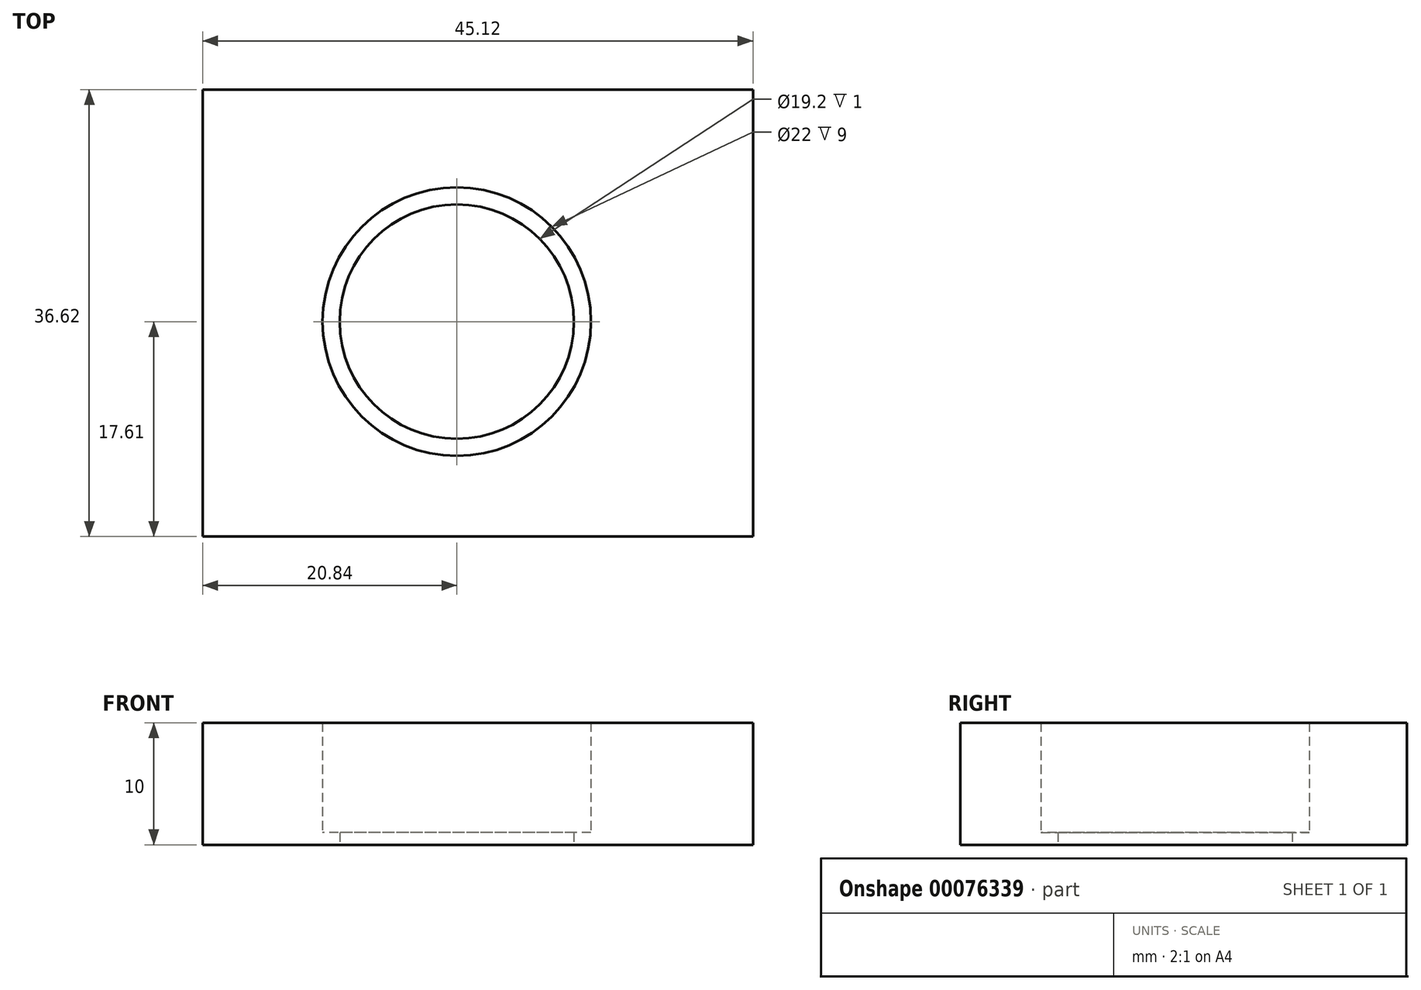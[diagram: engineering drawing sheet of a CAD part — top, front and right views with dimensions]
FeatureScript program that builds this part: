
annotation { "Feature Type Name" : "Feature", "Feature Type Description" : "" }
export const myFeature = defineFeature(function(context is Context, id is Id, definition is map)
    precondition{}
    {
        {
            var Q0;
            Q0=qCreatedBy(makeId("Top.planeOp"),FACE);
            var sketch = newSketch(context, id + "F0", { "sketchPlane" : qUnion([Q0])});
            skCircle(sketch, "E0.0", {"center": v(0, 0) * mm, "radius": 9.6 * mm});
            skLineSegment(sketch, "E1.bottom", {"start": v(-20.84, -17.61) * mm, "end": v(24.28, -17.61) * mm});
            skLineSegment(sketch, "E1.top", {"start": v(-20.84, 19) * mm, "end": v(24.28, 19) * mm});
            skLineSegment(sketch, "E1.left", {"start": v(-20.84, -17.61) * mm, "end": v(-20.84, 19) * mm});
            skLineSegment(sketch, "E1.right", {"start": v(24.28, -17.61) * mm, "end": v(24.28, 19) * mm});
            skCircle(sketch, "E2.0", {"center": v(0, 0) * mm, "radius": 11 * mm});
            skSolve(sketch);
        }
        {
            var Q0;
            Q0=makeQuery(id+"F0.imprint","IMPRINT",FACE,{"disambiguationData":[TD([[makeQuery(id+"F0.imprint","IMPRINT",EDGE,{"derivedFrom":sQuery(id+"F0.wireOp",EDGE,"E0.0")}),-1.0]])]});
            extrude(context, id + "F1", {"entities" : qUnion([Q0]), "depth" : 1 * mm});
        }
        {
            var Q0;
            Q0=makeQuery(id+"F0.imprint","IMPRINT",FACE,{"disambiguationData":[TD([[makeQuery(id+"F0.imprint","IMPRINT",EDGE,{"derivedFrom":sQuery(id+"F0.wireOp",EDGE,"E1.bottom")}),1.0]])]});
            extrude(context, id + "F2", {"entities" : qUnion([Q0]), "operationType" : NewBodyOperationType.ADD, "depth" : 10 * mm});
        }
    });
